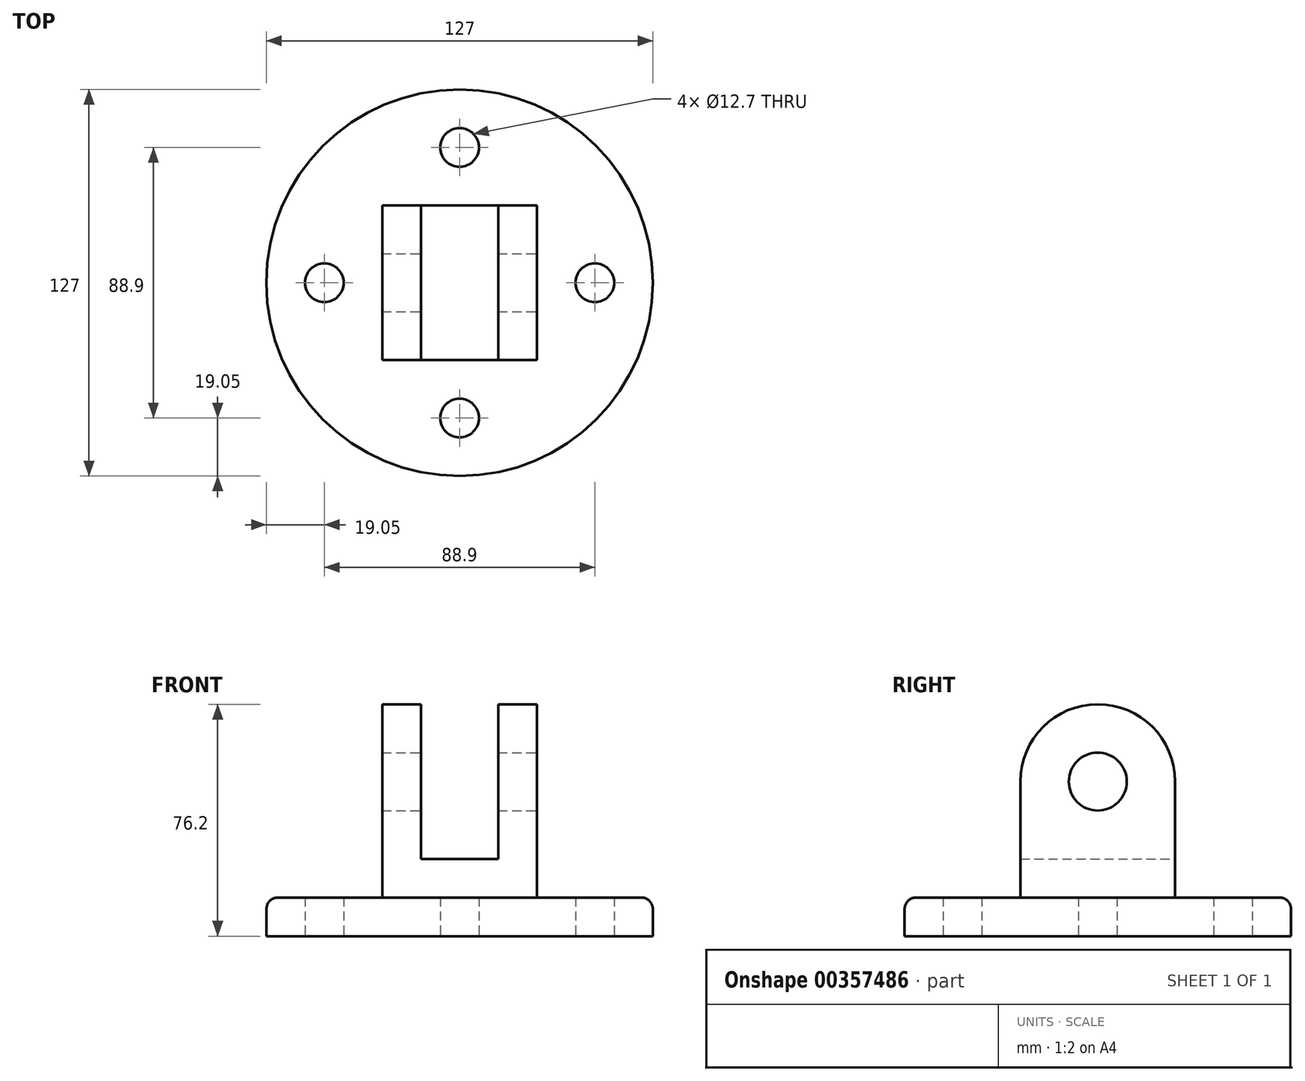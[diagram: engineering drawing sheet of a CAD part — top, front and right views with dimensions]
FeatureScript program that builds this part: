
annotation { "Feature Type Name" : "Feature", "Feature Type Description" : "" }
export const myFeature = defineFeature(function(context is Context, id is Id, definition is map)
    precondition{}
    {
        {
            var Q0;
            Q0=qCreatedBy(makeId("Top.planeOp"),FACE);
            var sketch = newSketch(context, id + "F0", { "sketchPlane" : qUnion([Q0])});
            skCircle(sketch, "E0", {"center": v(0, 0) * mm, "radius": 63.5 * mm});
            skCircle(sketch, "E1", {"center": v(0, 0) * mm, "radius": 44.45 * mm, "construction": true});
            skCircle(sketch, "E2", {"center": v(0, 44.45) * mm, "radius": 6.35 * mm});
            skCircle(sketch, "E3", {"center": v(44.45, 0) * mm, "radius": 6.35 * mm});
            skCircle(sketch, "E4", {"center": v(0, -44.45) * mm, "radius": 6.35 * mm});
            skCircle(sketch, "E5", {"center": v(-44.45, 0) * mm, "radius": 6.35 * mm});
            skSolve(sketch);
        }
        {
            var Q0;
            Q0 = qSketchRegion(id + "F0", true);
            extrude(context, id + "F1", {"entities" : qUnion([Q0]), "depth" : 12.7 * mm});
        }
        {
            var Q0;
            Q0=makeQuery(id+"F1.opExtrude","CAP_EDGE",EDGE,{"disambiguationData":[OSD([sQuery(id+"F0.wireOp",EDGE,"E0")])],"isStart":false});
            fillet(context, id + "F2", {"entities" : qUnion([Q0]), "radius" : 3.8 * mm, "tangentPropagation" : true, "allowEdgeOverflow" : false});
        }
        {
            var Q0;
            Q0=qCreatedBy(makeId("Front.planeOp"),FACE);
            var sketch = newSketch(context, id + "F3", { "sketchPlane" : qUnion([Q0])});
            skLineSegment(sketch, "E6.0", {"start": v(-25.4, 12.7) * mm, "end": v(25.4, 12.7) * mm});
            skLineSegment(sketch, "E7", {"start": v(25.4, 12.7) * mm, "end": v(25.4, 76.2) * mm});
            skLineSegment(sketch, "E8", {"start": v(25.4, 76.2) * mm, "end": v(12.7, 76.2) * mm});
            skLineSegment(sketch, "E9", {"start": v(12.7, 76.2) * mm, "end": v(12.7, 25.4) * mm});
            skLineSegment(sketch, "E10", {"start": v(12.7, 25.4) * mm, "end": v(-12.7, 25.4) * mm});
            skLineSegment(sketch, "E11", {"start": v(-12.7, 25.4) * mm, "end": v(-12.7, 76.2) * mm});
            skLineSegment(sketch, "E12", {"start": v(-12.7, 76.2) * mm, "end": v(-25.4, 76.2) * mm});
            skLineSegment(sketch, "E13", {"start": v(-25.4, 76.2) * mm, "end": v(-25.4, 12.7) * mm});
            skSolve(sketch);
        }
        {
            var Q0;
            Q0 = qSketchRegion(id + "F3", true);
            extrude(context, id + "F4", {"entities" : qUnion([Q0]), "operationType" : NewBodyOperationType.ADD, "endBound" : BoundingType.SYMMETRIC, "depth" : 50.8 * mm});
        }
        {
            var Q0;
            Q0=makeQuery(id+"F4.opExtrude","SWEPT_FACE",FACE,{"disambiguationData":[OSD([sQuery(id+"F3.wireOp",EDGE,"E7")])]});
            var sketch = newSketch(context, id + "F5", { "sketchPlane" : qUnion([Q0])});
            skCircle(sketch, "E14", {"center": v(0, 50.8) * mm, "radius": 9.53 * mm});
            skLineSegment(sketch, "E15.0.0", {"start": v(25.4, 50.8) * mm, "end": v(25.4, 76.2) * mm});
            skLineSegment(sketch, "E15.0.1", {"start": v(25.4, 76.2) * mm, "end": v(-25.4, 76.2) * mm});
            skLineSegment(sketch, "E15.0.2", {"start": v(-25.4, 76.2) * mm, "end": v(-25.4, 50.8) * mm});
            skLineSegment(sketch, "E15.0.3", {"start": v(-25.4, 12.7) * mm, "end": v(25.4, 12.7) * mm});
            skArc(sketch, "E16", {"start": v(25.4, 50.8) * mm, "mid": v(0, 76.2) * mm, "end": v(-25.4, 50.8) * mm});
            skSolve(sketch);
        }
        {
            var Q0;
            Q0 = qSketchRegion(id + "F5", true);
            extrude(context, id + "F6", {"entities" : qUnion([Q0]), "operationType" : NewBodyOperationType.REMOVE, "endBound" : BoundingType.THROUGH_ALL, "oppositeDirection" : true, "depth" : 25.4 * mm});
        }
    });
